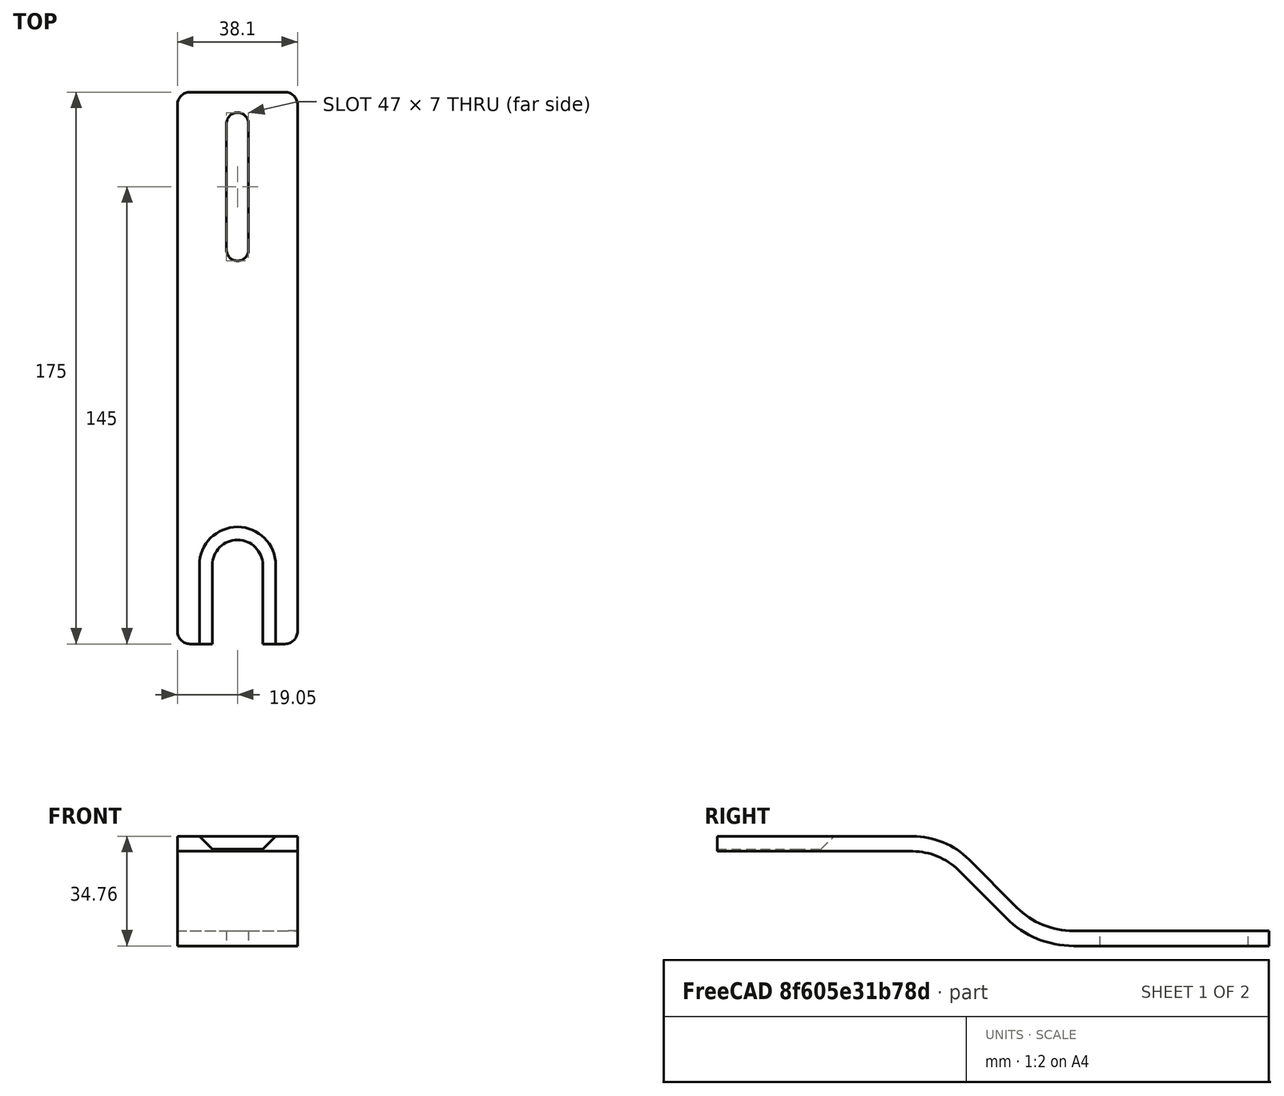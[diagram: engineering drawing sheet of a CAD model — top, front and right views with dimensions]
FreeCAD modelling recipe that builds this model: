
FCSTD DOCUMENT  (FreeCAD 0.19R23578 (Git))
Label: heated_bed_bracket
License: All rights reserved
LicenseURL: http://en.wikipedia.org/wiki/All_rights_reserved
objects: TechDraw::DrawViewDimension×8, Sketcher::SketchObject×4, TechDraw::DrawProjGroupItem×3, TechDraw::DrawViewDimExtent×3, PartDesign::Pocket×2, PartDesign::AdditivePipe×1, PartDesign::Chamfer×1, PartDesign::Fillet×1, PartDesign::Body×1, TechDraw::DrawSVGTemplate×1, TechDraw::DrawViewPart×1, TechDraw::DrawProjGroup×1, TechDraw::DrawPage×1
note: 15 computed .brp shape members not serialized (recipe doc carries the construction recipe); baked Part::Feature solids carry a one-line shape summary decoded from their .brp

FEATURE [Sketcher::SketchObject] Sketch015
  MapMode = 5
  Placement = pos=(0,0,0) rot=(0.57735,0.57735,0.57735;2.0944rad)
  Support = -> [YZ_Plane019]
  sketch-geometry (5):
    g0: LineSegment StartX=0 StartY=0 StartZ=0 EndX=61.979 EndY=0 EndZ=0
    g1: LineSegment StartX=113.021 StartY=-30 StartZ=0 EndX=175 EndY=-30 EndZ=0
    g2: LineSegment StartX=79.9395 StartY=-7.43949 StartZ=0 EndX=95.0605 EndY=-22.5605 EndZ=0
    g3: ArcOfCircle CenterX=61.979 CenterY=-25.4 CenterZ=0 NormalX=0 NormalY=0 NormalZ=1 AngleXU=0 Radius=25.4 StartAngle=0.785398 EndAngle=1.5708
    g4: ArcOfCircle CenterX=113.021 CenterY=-4.6 CenterZ=0 NormalX=0 NormalY=0 NormalZ=1 AngleXU=0 Radius=25.4 StartAngle=3.92699 EndAngle=4.71239
  constraints (13):
    c: Coincident(g0,g-1)
    c: Horizontal(g1)
    c: Tangent(g0,g3) = 1.5708
    c: Tangent(g2,g3) = 1.5708
    c: Tangent(g2,g4) = -1.5708
    c: Tangent(g1,g4) = -1.5708
    c: Equal(g3,g4)
    c: Horizontal(g0)
    c: Equal(g0,g1)
    c: DistanceY(g1,g0) = 30
    c: DistanceX(g0,g1) = 175
    c: Radius(g3) = 25.4
    c: Angle(g0,g2) = 2.35619
FEATURE [Sketcher::SketchObject] Sketch016
  MapMode = 5
  Support = -> [XY_Plane019]
  sketch-geometry (4):
    g0: ArcOfCircle CenterX=0 CenterY=0 CenterZ=0 NormalX=0 NormalY=0 NormalZ=1 AngleXU=0 Radius=8 StartAngle=3.14159 EndAngle=6.28319
    g1: ArcOfCircle CenterX=-2e-16 CenterY=25 CenterZ=0 NormalX=0 NormalY=0 NormalZ=1 AngleXU=0 Radius=8 StartAngle=0 EndAngle=3.14159
    g2: LineSegment StartX=8 StartY=-2e-15 StartZ=0 EndX=8 EndY=25 EndZ=0
    g3: LineSegment StartX=-8 StartY=-2.6e-15 StartZ=0 EndX=-8 EndY=25 EndZ=0
  constraints (9):
    c: Tangent(g0,g3) = 1.5708
    c: Tangent(g0,g2) = -1.5708
    c: Tangent(g2,g1) = -1.5708
    c: Tangent(g3,g1) = 1.5708
    c: Vertical(g2)
    c: Equal(g0,g1)
    c: Coincident(g0,g-1)
    c: Diameter(g1) = 16
    c: DistanceY(g0,g1) = 25
FEATURE [Sketcher::SketchObject] Sketch017
  MapMode = 5
  Support = -> [XY_Plane019]
  sketch-geometry (4):
    g0: ArcOfCircle CenterX=0 CenterY=125 CenterZ=0 NormalX=0 NormalY=0 NormalZ=1 AngleXU=0 Radius=3.5 StartAngle=3.14159 EndAngle=6.28319
    g1: ArcOfCircle CenterX=-6.15e-14 CenterY=165 CenterZ=0 NormalX=0 NormalY=0 NormalZ=1 AngleXU=0 Radius=3.5 StartAngle=-3.73e-14 EndAngle=3.14159
    g2: LineSegment StartX=3.5 StartY=125 StartZ=0 EndX=3.5 EndY=165 EndZ=0
    g3: LineSegment StartX=-3.5 StartY=125 StartZ=0 EndX=-3.5 EndY=165 EndZ=0
  constraints (10):
    c: Tangent(g0,g3) = 1.5708
    c: Tangent(g0,g2) = -1.5708
    c: Tangent(g2,g1) = -1.5708
    c: Tangent(g3,g1) = 1.5708
    c: Vertical(g2)
    c: Equal(g0,g1)
    c: PointOnObject(g0,g-2)
    c: DistanceY(g-1,g0) = 125
    c: DistanceY(g-1,g1) = 165
    c: Diameter(g1) = 7
FEATURE [Sketcher::SketchObject] Sketch003
  MapMode = 5
  Placement = pos=(0,0,0) rot=(1,0,0;1.5708rad)
  Support = -> [XZ_Plane019]
  sketch-geometry (4):
    g0: LineSegment StartX=-19.05 StartY=0 StartZ=0 EndX=19.05 EndY=0 EndZ=0
    g1: LineSegment StartX=19.05 StartY=0 StartZ=0 EndX=19.05 EndY=-4.7625 EndZ=0
    g2: LineSegment StartX=19.05 StartY=-4.7625 StartZ=0 EndX=-19.05 EndY=-4.7625 EndZ=0
    g3: LineSegment StartX=-19.05 StartY=-4.7625 StartZ=0 EndX=-19.05 EndY=0 EndZ=0
  constraints (12):
    c: Coincident(g0,g1)
    c: Coincident(g1,g2)
    c: Coincident(g2,g3)
    c: Coincident(g3,g0)
    c: Horizontal(g0)
    c: Horizontal(g2)
    c: Vertical(g1)
    c: Vertical(g3)
    c: PointOnObject(g0,g-1)
    c: DistanceX(g0,g0) = 38.1
    c: DistanceX(g-1,g0) = 19.05
    c: DistanceY(g1,g1) = 4.7625
FEATURE [PartDesign::AdditivePipe] AdditivePipe
  AllowMultiFace = false
  AuxilleryCurvelinear = true
  AuxillerySpineTangent = false
  Binormal = (0,0,0)
  Mode = 2
  Placement = pos=(0,0,0) rot=(1,0,0;1.5708rad)
  Profile = -> Sketch003
  Spine = -> Sketch015 [Edge1,Edge2,Edge3,Edge4,Edge5]
  SpineTangent = false
  Transformation = 0
  Transition = 0
FEATURE [PartDesign::Pocket] Pocket007
  AllowMultiFace = false
  BaseFeature = -> AdditivePipe
  Length = 5
  Length2 = 100
  Placement = pos=(0,0,0) rot=(1,0,0;1.5708rad)
  Profile = -> Sketch016
  Type = 1
FEATURE [PartDesign::Chamfer] Chamfer
  Angle = 45
  Base = -> Pocket007 [Edge14,Edge20,Edge19]
  BaseFeature = -> Pocket007
  ChamferType = 0
  FlipDirection = false
  Placement = pos=(0,0,0) rot=(1,0,0;1.5708rad)
  Size = 4.1
  Size2 = 1
  SupportTransform = true
FEATURE [PartDesign::Pocket] Pocket008
  BaseFeature = -> Chamfer
  Length = 5
  Length2 = 100
  Placement = pos=(0,0,0) rot=(1,0,0;1.5708rad)
  Profile = -> Sketch017
  Type = 1
FEATURE [PartDesign::Fillet] Fillet
  Base = -> Pocket008 [Edge5,Edge27,Edge70,Edge71]
  BaseFeature = -> Pocket008
  Placement = pos=(0,0,0) rot=(1,0,0;1.5708rad)
  Radius = 4
  SupportTransform = true
FEATURE [PartDesign::Body] Body003  label="heated_bed_bracket"
  Group = -> [Sketch003,Sketch015,AdditivePipe,Sketch016,Pocket007,Chamfer,Sketch017,Pocket008,Fillet]
  Origin = -> Origin019
  Tip = -> Fillet
FEATURE [TechDraw::DrawSVGTemplate] Template006
  EditableTexts = Author=Alex Neufeld; DWG_num=2020-101; Date=15/05/2020; Revision=2; Scale=NTS; Subtitle=3 Req.; Title=Heated Bed Support Bracket
  Height = 215.9
  Orientation = 1
  Width = 279.4
FEATURE [TechDraw::DrawViewPart] View007
  CoarseView = false
  Direction = (0.577,-0.577,0.577)
  Focus = 100
  HardHidden = false
  IsoCount = 0
  IsoHidden = false
  IsoVisible = false
  LockPosition = true
  Perspective = false
  Rotation = 0
  Scale = 0.5
  ScaleType = 2
  SeamHidden = false
  SeamVisible = true
  SmoothHidden = false
  SmoothVisible = true
  Source = -> [Body003]
  X = 49.5472
  XDirection = (0.707,0.707,0)
  Y = 186.724
FEATURE [TechDraw::DrawProjGroupItem] ProjItem023  label="Front006"
  CoarseView = false
  Direction = (0,0,1)
  Focus = 100
  HardHidden = false
  IsoCount = 0
  IsoHidden = false
  IsoVisible = false
  LockPosition = true
  Perspective = false
  Rotation = 0
  RotationVector = (1,0,0)
  ScaleType = 2
  SeamHidden = false
  SeamVisible = true
  SmoothHidden = false
  SmoothVisible = true
  Source = -> [Body003]
  Type = 0
  X = 0
  XDirection = (1e-16,-1,0)
  Y = 0
FEATURE [TechDraw::DrawProjGroupItem] ProjItem024  label="Bottom005"
  CoarseView = false
  Direction = (-1,-1e-16,0)
  Focus = 100
  HardHidden = false
  IsoCount = 0
  IsoHidden = false
  IsoVisible = false
  LockPosition = true
  Perspective = false
  Rotation = 0
  RotationVector = (1,0,0)
  ScaleType = 2
  SeamHidden = false
  SeamVisible = true
  SmoothHidden = false
  SmoothVisible = true
  Source = -> [Body003]
  Type = 5
  X = 0
  XDirection = (1e-16,-1,0)
  Y = 53.1
FEATURE [TechDraw::DrawProjGroupItem] ProjItem025  label="Right002"
  CoarseView = false
  Direction = (1e-16,-1,1e-16)
  Focus = 100
  HardHidden = false
  IsoCount = 0
  IsoHidden = false
  IsoVisible = false
  LockPosition = true
  Perspective = false
  Rotation = 0
  RotationVector = (1,0,0)
  ScaleType = 2
  SeamHidden = false
  SeamVisible = true
  SmoothHidden = false
  SmoothVisible = true
  Source = -> [Body003]
  Type = 2
  X = -122.429
  XDirection = (0,-1e-16,-1)
  Y = 0
FEATURE [TechDraw::DrawProjGroup] ProjGroup006
  Anchor = -> ProjItem023
  AutoDistribute = true
  LockPosition = false
  ProjectionType = 0
  Rotation = 0
  ScaleType = 0
  Source = -> [Body003]
  Views = -> [ProjItem023,ProjItem024,ProjItem025]
  X = 163.157
  Y = 88.6941
  spacingX = 15
  spacingY = 15
FEATURE [TechDraw::DrawViewDimExtent] DimExtent002
  Arbitrary = false
  ArbitraryTolerances = false
  CosmeticTags = 40a776e2-5fee-4af6-bf52-77ef4ba42de3 | 3502933f-edae-4da0-bb0d-b59fe228f185
  DirExtent = 1
  FormatSpec = %.1f
  FormatSpecOverTolerance = %+.2f
  FormatSpecUnderTolerance = %+.2f
  Inverted = false
  LockPosition = false
  MeasureType = 1
  OverTolerance = 0
  References2D = -> [ProjItem024]
  Rotation = 0
  ScaleType = 0
  Source = -> [ProjItem024]
  TheoreticalExact = false
  Type = 2
  UnderTolerance = 0
  X = 93.829
  Y = -3.15097
FEATURE [TechDraw::DrawViewDimExtent] DimExtent003
  Arbitrary = false
  ArbitraryTolerances = false
  CosmeticTags = 56a5d33d-48c1-42c5-9a55-81271bc0a9cf | 7367f88c-4bb7-4e22-a4a2-363c2dde8282
  DirExtent = 0
  FormatSpec = %.1f
  FormatSpecOverTolerance = %+.2f
  FormatSpecUnderTolerance = %+.2f
  Inverted = false
  LockPosition = false
  MeasureType = 1
  OverTolerance = 0
  References2D = -> [ProjItem024]
  Rotation = 0
  ScaleType = 0
  Source = -> [ProjItem024]
  TheoreticalExact = false
  Type = 1
  UnderTolerance = 0
  X = 4.5514
  Y = 26.6082
FEATURE [TechDraw::DrawViewDimension] Dimension114
  Arbitrary = false
  ArbitraryTolerances = false
  FormatSpec = %.1f
  FormatSpecOverTolerance = %+.2f
  FormatSpecUnderTolerance = %+.2f
  Inverted = false
  LockPosition = false
  MeasureType = 1
  OverTolerance = 0
  References2D = -> [ProjItem023]
  Rotation = 0
  ScaleType = 0
  TheoreticalExact = false
  Type = 1
  UnderTolerance = 0
  X = 75
  Y = -8
FEATURE [TechDraw::DrawViewDimension] Dimension115
  Arbitrary = false
  ArbitraryTolerances = false
  FormatSpec = %.1f
  FormatSpecOverTolerance = %+.2f
  FormatSpecUnderTolerance = %+.2f
  Inverted = false
  LockPosition = false
  MeasureType = 1
  OverTolerance = 0
  References2D = -> [ProjItem023]
  Rotation = 0
  ScaleType = 0
  TheoreticalExact = false
  Type = 2
  UnderTolerance = 0
  X = 40.6182
  Y = 0.972523
FEATURE [TechDraw::DrawViewDimension] Dimension116
  Arbitrary = false
  ArbitraryTolerances = false
  FormatSpec = %.1f
  FormatSpecOverTolerance = %+.2f
  FormatSpecUnderTolerance = %+.2f
  Inverted = false
  LockPosition = false
  MeasureType = 1
  OverTolerance = 0
  References2D = -> [ProjItem025]
  Rotation = 0
  ScaleType = 0
  TheoreticalExact = false
  Type = 2
  UnderTolerance = 0
  X = -0.307206
  Y = 0.729392
FEATURE [TechDraw::DrawViewDimExtent] DimExtent004
  Arbitrary = false
  ArbitraryTolerances = false
  CosmeticTags = 63ff5876-13bd-4040-85b2-fb7422d9c357 | 3d9a6e47-d91b-4086-bc29-d26c843bf4b5
  DirExtent = 1
  FormatSpec = %.1f
  FormatSpecOverTolerance = %+.2f
  FormatSpecUnderTolerance = %+.2f
  Inverted = false
  LockPosition = false
  MeasureType = 1
  OverTolerance = 0
  References2D = -> [ProjItem025]
  Rotation = 0
  ScaleType = 0
  Source = -> [ProjItem025]
  TheoreticalExact = false
  Type = 2
  UnderTolerance = 0
  X = 23.3405
  Y = -0.729392
FEATURE [TechDraw::DrawViewDimension] Dimension117
  Arbitrary = false
  ArbitraryTolerances = false
  FormatSpec = R%.1f
  FormatSpecOverTolerance = %+.2f
  FormatSpecUnderTolerance = %+.2f
  Inverted = false
  LockPosition = false
  MeasureType = 1
  OverTolerance = 0
  References2D = -> [ProjItem024]
  Rotation = 0
  ScaleType = 0
  TheoreticalExact = false
  Type = 4
  UnderTolerance = 0
  X = -23.8268
  Y = 4.86261
FEATURE [TechDraw::DrawViewDimension] Dimension118
  Arbitrary = false
  ArbitraryTolerances = false
  FormatSpec = R%.1f
  FormatSpecOverTolerance = %+.2f
  FormatSpecUnderTolerance = %+.2f
  Inverted = false
  LockPosition = false
  MeasureType = 1
  OverTolerance = 0
  References2D = -> [ProjItem023]
  Rotation = 0
  ScaleType = 0
  TheoreticalExact = false
  Type = 4
  UnderTolerance = 0
  X = -92.1465
  Y = -26.015
FEATURE [TechDraw::DrawViewDimension] Dimension119
  Arbitrary = false
  ArbitraryTolerances = false
  FormatSpec = %.1f
  FormatSpecOverTolerance = %+.2f
  FormatSpecUnderTolerance = %+.2f
  Inverted = false
  LockPosition = false
  MeasureType = 1
  OverTolerance = 0
  References2D = -> [ProjItem023]
  Rotation = 0
  ScaleType = 0
  TheoreticalExact = false
  Type = 1
  UnderTolerance = 0
  X = -57.2569
  Y = -7.05079
FEATURE [TechDraw::DrawViewDimension] Dimension120
  Arbitrary = false
  ArbitraryTolerances = false
  FormatSpec = %.1f
  FormatSpecOverTolerance = %+.2f
  FormatSpecUnderTolerance = %+.2f
  Inverted = false
  LockPosition = false
  MeasureType = 1
  OverTolerance = 0
  References2D = -> [ProjItem023]
  Rotation = 0
  ScaleType = 0
  TheoreticalExact = false
  Type = 1
  UnderTolerance = 0
  X = -76.713
  Y = 9.9804
FEATURE [TechDraw::DrawViewDimension] Dimension121
  Arbitrary = false
  ArbitraryTolerances = false
  FormatSpec = %.1f
  FormatSpecOverTolerance = %+.2f
  FormatSpecUnderTolerance = %+.2f
  Inverted = false
  LockPosition = false
  MeasureType = 1
  OverTolerance = 0
  References2D = -> [ProjItem025]
  Rotation = 0
  ScaleType = 0
  TheoreticalExact = false
  Type = 6
  UnderTolerance = 0
  X = -23.9191
  Y = 0.11725
FEATURE [TechDraw::DrawPage] Page006  label="heated_bed_bracket_dwg"
  KeepUpdated = false
  NextBalloonIndex = 1
  ProjectionType = 0
  Template = -> Template006
  Views = -> [View007,ProjGroup006,DimExtent002,DimExtent003,Dimension114,Dimension115,Dimension116,DimExtent004,Dimension117,Dimension118,Dimension119,Dimension120,Dimension121]
